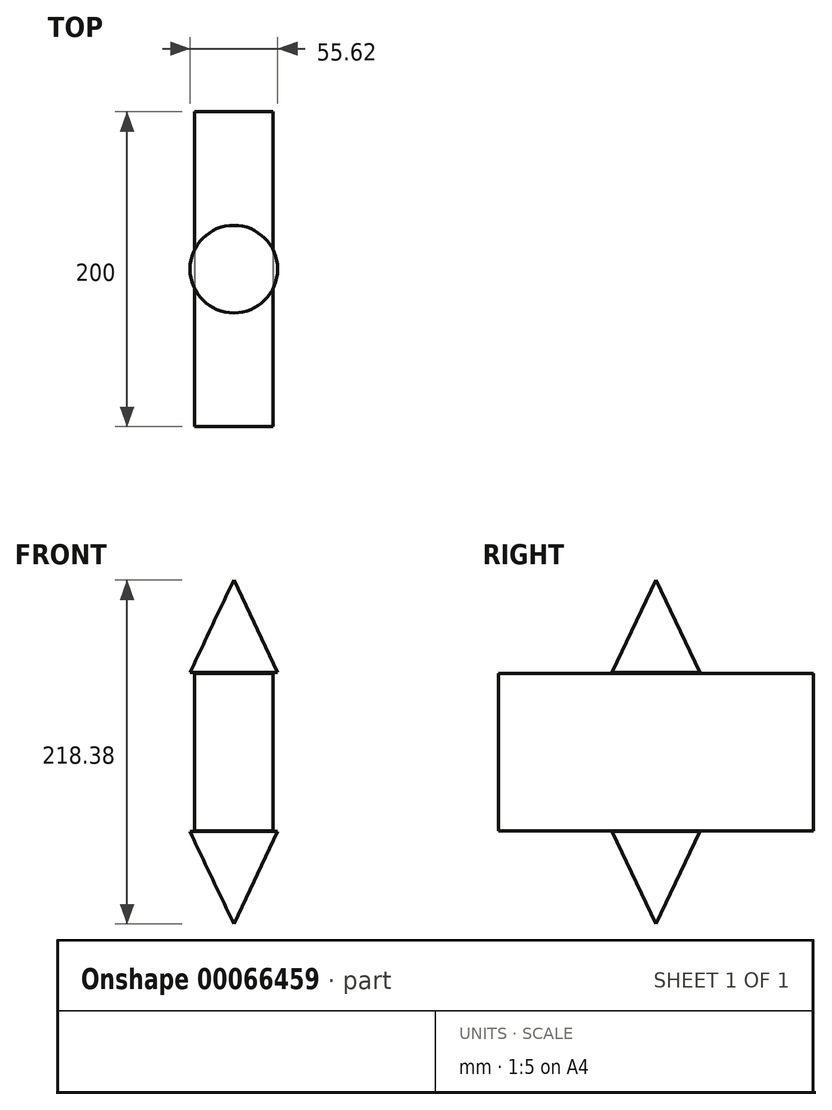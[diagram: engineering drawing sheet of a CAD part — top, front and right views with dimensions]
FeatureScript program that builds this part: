
annotation { "Feature Type Name" : "Feature", "Feature Type Description" : "" }
export const myFeature = defineFeature(function(context is Context, id is Id, definition is map)
    precondition{}
    {
        {
            var Q0;
            Q0=qCreatedBy(makeId("Right.planeOp"),FACE);
            var sketch = newSketch(context, id + "F0", { "sketchPlane" : qUnion([Q0])});
            skLineSegment(sketch, "E0.rect.bottom", {"start": v(100, 50) * mm, "end": v(-100, 50) * mm});
            skLineSegment(sketch, "E0.rect.top", {"start": v(100, -50) * mm, "end": v(-100, -50) * mm});
            skLineSegment(sketch, "E0.rect.left", {"start": v(100, 50) * mm, "end": v(100, -50) * mm});
            skLineSegment(sketch, "E0.rect.right", {"start": v(-100, 50) * mm, "end": v(-100, -50) * mm});
            skPoint(sketch, "E0.rect.middle", {"position": v(0, 0) * mm});
            skSolve(sketch);
        }
        {
            var Q0;
            Q0 = qSketchRegion(id + "F0", true);
            extrude(context, id + "F1", {"entities" : qUnion([Q0]), "endBound" : BoundingType.SYMMETRIC, "depth" : 50 * mm});
        }
        {
            var Q0;
            Q0=qCreatedBy(makeId("Right.planeOp"),FACE);
            var sketch = newSketch(context, id + "F2", { "sketchPlane" : qUnion([Q0])});
            skLineSegment(sketch, "E1", {"start": v(0, 50.6) * mm, "end": v(0, 109.19) * mm});
            skLineSegment(sketch, "E2", {"start": v(0, 109.19) * mm, "end": v(-27.8, 50.6) * mm});
            skLineSegment(sketch, "E3", {"start": v(-27.8, 50.6) * mm, "end": v(0, 50.6) * mm});
            skSolve(sketch);
        }
        {
            var Q0;
            Q0 = qSketchRegion(id + "F2", true);
            var Q1;
            Q1=sQuery(id+"F2.wireOp",EDGE,"E1");
            revolve(context, id + "F3", {"entities" : qUnion([Q0]), "axis" : qUnion([Q1]), "revolveType" : RevolveType.FULL});
        }
        {
            var Q0;
            Q0=makeQuery(id+"F3.opRevolve","SWEPT_BODY",BODY,{"disambiguationData":[OSD([sQuery(id+"F2.wireOp",EDGE,"E1"),sQuery(id+"F2.wireOp",EDGE,"E2"),sQuery(id+"F2.wireOp",EDGE,"E3")])]});
            var Q1;
            Q1=qCreatedBy(makeId("Top.planeOp"),FACE);
            mirror(context, id + "F4", {"entities" : qUnion([Q0]), "mirrorPlane" : qUnion([Q1])});
        }
    });
